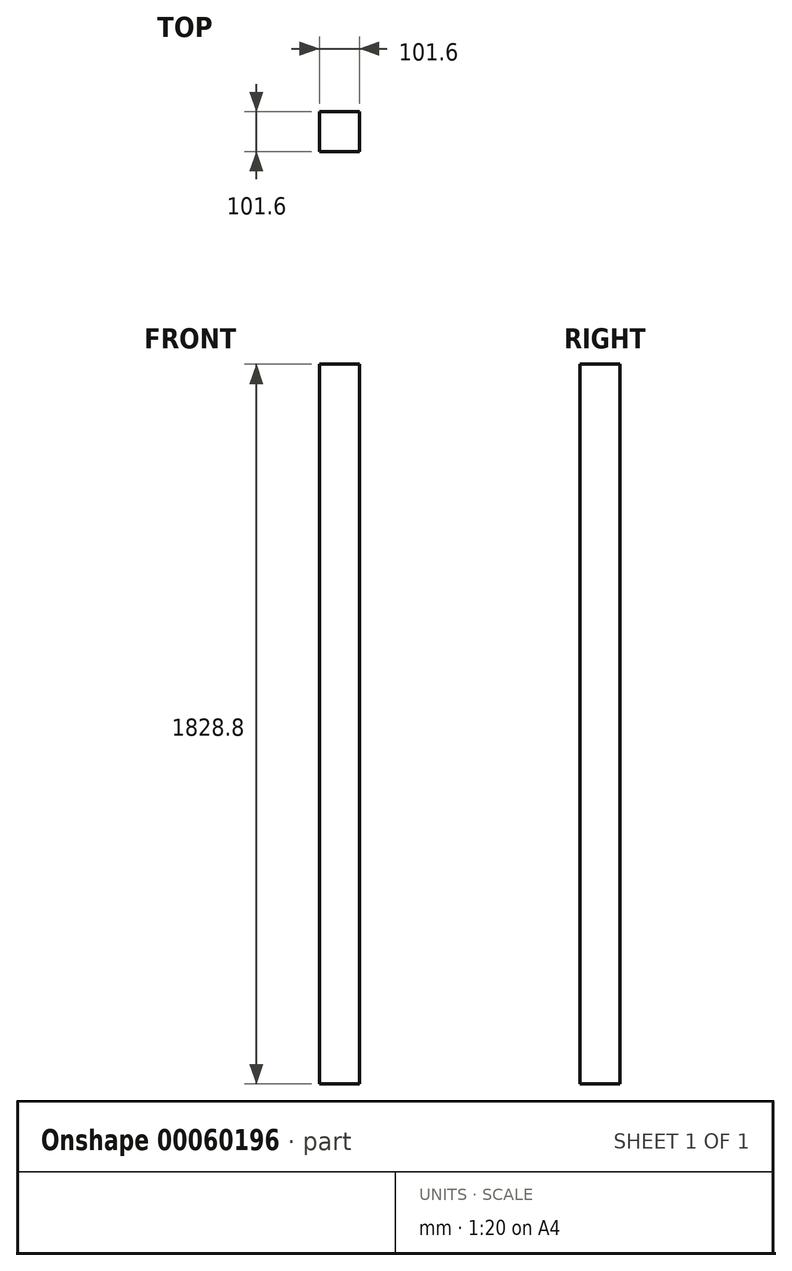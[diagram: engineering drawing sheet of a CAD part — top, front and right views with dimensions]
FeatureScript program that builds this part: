
annotation { "Feature Type Name" : "Feature", "Feature Type Description" : "" }
export const myFeature = defineFeature(function(context is Context, id is Id, definition is map)
    precondition{}
    {
        {
            var Q0;
            Q0=qCreatedBy(makeId("Top.planeOp"),FACE);
            var sketch = newSketch(context, id + "F0", { "sketchPlane" : qUnion([Q0])});
            skLineSegment(sketch, "E0.rect.bottom", {"start": v(50.8, 50.8) * mm, "end": v(-50.8, 50.8) * mm});
            skLineSegment(sketch, "E0.rect.top", {"start": v(50.8, -50.8) * mm, "end": v(-50.8, -50.8) * mm});
            skLineSegment(sketch, "E0.rect.left", {"start": v(50.8, 50.8) * mm, "end": v(50.8, -50.8) * mm});
            skLineSegment(sketch, "E0.rect.right", {"start": v(-50.8, 50.8) * mm, "end": v(-50.8, -50.8) * mm});
            skPoint(sketch, "E0.rect.middle", {"position": v(0, 0) * mm});
            skSolve(sketch);
        }
        {
            var Q0;
            Q0=makeQuery(id+"F0.imprint","IMPRINT",FACE,{"disambiguationData":[TD([[makeQuery(id+"F0.imprint","IMPRINT",EDGE,{"derivedFrom":sQuery(id+"F0.wireOp",EDGE,"E0.rect.bottom")}),1.0]])]});
            extrude(context, id + "F1", {"entities" : qUnion([Q0]), "depth" : 1828.8 * mm});
        }
    });
